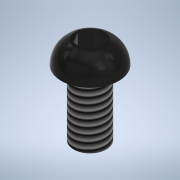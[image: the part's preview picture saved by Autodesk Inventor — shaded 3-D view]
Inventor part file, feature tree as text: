
AUTODESK INVENTOR PART (.ipt)
format: ipt  version: 2022 (Build 260153000, 153)  size: 154,112 bytes
history: native  units: mm
features: sketch x3, extrude x2, other x1, revolve x1, thread x1
ambient origin geometry x8: Origin, YZ Plane, XZ Plane, XY Plane, X Axis, Y Axis, Z Axis, Center Point
bodies: Body1 (feature_tree)
feature tree (8):
  other  "Твердое тело1"
  extrude  "Выдавливание1"  Depth=2.0mm
  revolve  "Вращение1"
  extrude  "Выдавливание2"  Depth=4.0mm TaperAngle=0.0deg
  thread  "Резьба1"
  sketch  "Эскиз1"
  sketch  "Эскиз2"
  sketch  "Эскиз3"
